# Revit family: ZF817-12
name_source: partatom
category: Plumbing Fixtures
units: mm (PartAtom-declared; Revit-internal decimal feet)

## family parameters
Always vertical = Yes
Cut with Voids When Loaded = No
Maintain Annotation Orientation = No
OmniClass Number = 23.70.50.21.24.14
OmniClass Title = Deck Waste Water Drains
Part Type = Normal
Room Calculation Point = No
Round Connector Dimension = Use Radius
Shared = No
Work Plane-Based = No

## types (5) — shared parameters
CW Connection = No
Default Elevation = 20 "
Description = 12 [305] x 24 [610] LONG REVEAL FIBER REINFORCED POLYMER CATCH BASIN
HW Connection = No
Main Material = Polymer - Zurn - Fiber Reinforced Blue
Manufacturer = Zurn Water, LLC
Manufacurer Brand = Zurn
Model = ZF812-12
Modified Date = 12/19/2025
Product Documentation Link = https://files.zurn.com
Product Page URL = https://www.zurn.com
Product data url = https://www.bimobject.com
URL = www.zurn.com
Vent Connection = No
WFU = 1
Waste Connection = Yes
zero-valued in all types: Body Height_E, CWFU, HWFU

## per-type parameters (varying)
| type | Assembly Code | Bottom Outlet | Connector Radius | End Outlet | Pipe Size_A Inside Diameter | Pipe Size_A Inside Radius | Pipe Size_A Nominal Diameter | Pipe Size_A Nominal Radius | Pipe Size_A Outer Diameter | Pipe Size_A Outer Radius | Type Comments |
| ZF812-12 With 4 Inch No Hub End Outlet | D2040300 | No | 2 " | Yes | 4.026 " | 2.013 " | 4 " | 2 " | 4.5 " | 2.25 " | ZF812-12 With 4 Inch No Hub End Outlet |
| ZF812-12 With 6 Inch No Hub End Outlet |  | No | 3 " | Yes | 6.065 " | 3.033 " | 6 " | 3 " | 6.625 " | 3.313 " | ZF812-12 With 6 Inch No Hub Bottom Outlet |
| ZF812-12 With 8 Inch No Hub End Outlet | D2040300 | No | 4 " | Yes | 7.981 " | 3.991 " | 8 " | 4 " | 8.625 " | 4.313 " | ZF812-12 With 8 Inch No Hub End Outlet |
| ZF812-12 With 4 Inch No Hub Bottom Outlet | D2040300 | Yes | 2 " | No | 4.026 " | 2.013 " | 4 " | 2 " | 4.5 " | 2.25 " | ZF812-12 With 4 Inch No Hub Bottom Outlet |
| ZF812-12 With 6 Inch No Hub Bottom Outlet | D2040300 | Yes | 3 " | No | 6.065 " | 3.033 " | 6 " | 3 " | 6.625 " | 3.313 " | ZF812-12 With 6 Inch No Hub End Outlet |

## geometry (parser evidence)
native form markers: Sweep x4
no freeform markers — native parametric forms only
